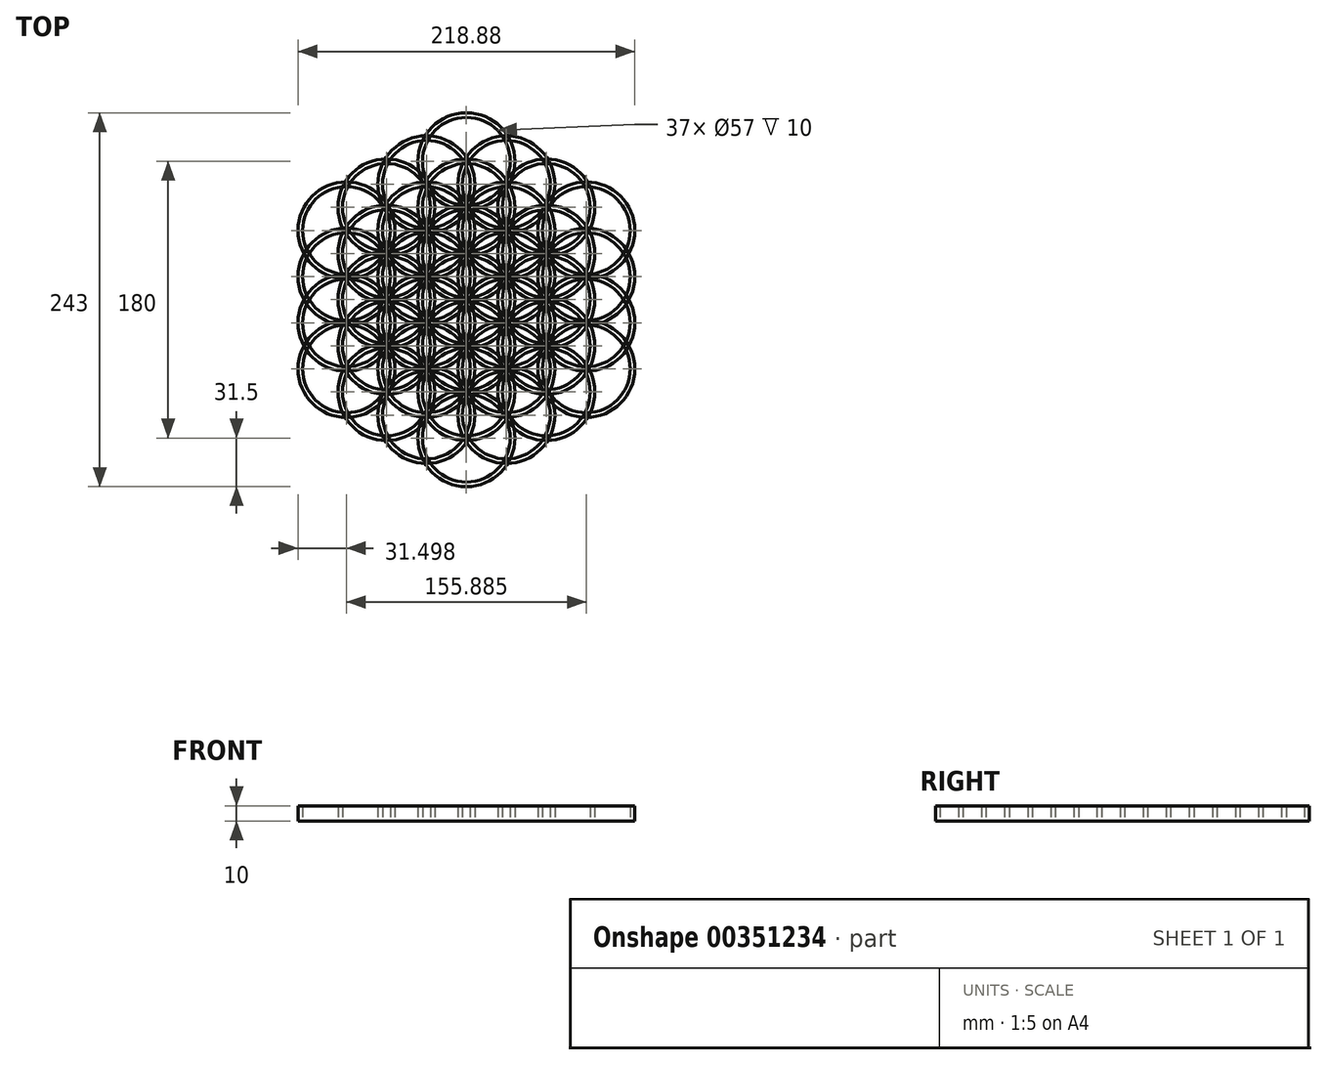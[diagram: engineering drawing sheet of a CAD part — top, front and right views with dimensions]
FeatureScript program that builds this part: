
annotation { "Feature Type Name" : "Feature", "Feature Type Description" : "" }
export const myFeature = defineFeature(function(context is Context, id is Id, definition is map)
    precondition{}
    {
        {
            var Q0;
            Q0=qCreatedBy(makeId("Right.planeOp"),FACE);
            var sketch = newSketch(context, id + "F0", { "sketchPlane" : qUnion([Q0])});
            skLineSegment(sketch, "E0", {"start": v(0, 0) * mm, "end": v(0, -9.37) * mm});
            skSolve(sketch);
        }
        {
            var Q0;
            Q0=qCreatedBy(makeId("Top.planeOp"),FACE);
            var sketch = newSketch(context, id + "F1", { "sketchPlane" : qUnion([Q0])});
            skCircle(sketch, "E1", {"center": v(0, 0) * mm, "radius": 30 * mm, "construction": true});
            skCircle(sketch, "E2.0", {"center": v(0, 0) * mm, "radius": 31.5 * mm});
            skCircle(sketch, "E3.0", {"center": v(0, 0) * mm, "radius": 28.5 * mm});
            skSolve(sketch);
        }
        {
            var Q0;
            Q0=makeQuery(id+"F1.imprint","IMPRINT",FACE,{"disambiguationData":[TD([[makeQuery(id+"F1.imprint","IMPRINT",EDGE,{"derivedFrom":sQuery(id+"F1.wireOp",EDGE,"E2.0")}),1.0]])]});
            extrude(context, id + "F2", {"entities" : qUnion([Q0]), "depth" : 10 * mm});
        }
        {
            var Q0;
            Q0=qCreatedBy(makeId("Top.planeOp"),FACE);
            var sketch = newSketch(context, id + "F3", { "sketchPlane" : qUnion([Q0])});
            skCircle(sketch, "E4", {"center": v(0, 30) * mm, "radius": 30 * mm, "construction": true});
            skCircle(sketch, "E5.0", {"center": v(0, 30) * mm, "radius": 31.5 * mm});
            skCircle(sketch, "E6.0", {"center": v(0, 30) * mm, "radius": 28.5 * mm});
            skCircle(sketch, "E7", {"center": v(0, 0) * mm, "radius": 30 * mm, "construction": true});
            skCircle(sketch, "E8.0", {"center": v(0, 0) * mm, "radius": 31.5 * mm, "construction": true});
            skCircle(sketch, "E9.0", {"center": v(0, 0) * mm, "radius": 28.5 * mm, "construction": true});
            skSolve(sketch);
        }
        {
            var Q0;
            Q0=qSketchRegion(id+"F3",true);
            extrude(context, id + "F4", {"entities" : qUnion([Q0]), "depth" : 10 * mm});
        }
        {
            var Q0;
            Q0=makeQuery(id+"F4.opExtrude","SWEPT_BODY",BODY,{"disambiguationData":[OSD([sQuery(id+"F3.wireOp",EDGE,"E5.0"),sQuery(id+"F3.wireOp",EDGE,"E6.0")])]});
            var Q1;
            Q1=sQuery(id+"F0.wireOp",EDGE,"E0");
            circularPattern(context, id + "F5", {"entities" : qUnion([Q0]), "axis" : qUnion([Q1]), "angle" : 360 * degree, "instanceCount" : 6, "equalSpace" : true});
        }
        {
            var Q0;
            Q0=qCreatedBy(makeId("Top.planeOp"),FACE);
            var sketch = newSketch(context, id + "F6", { "sketchPlane" : qUnion([Q0])});
            skCircle(sketch, "E10", {"center": v(0, 0) * mm, "radius": 30 * mm, "construction": true});
            skCircle(sketch, "E11.0", {"center": v(0, 0) * mm, "radius": 31.5 * mm, "construction": true});
            skCircle(sketch, "E12.0", {"center": v(0, 0) * mm, "radius": 28.5 * mm, "construction": true});
            skCircle(sketch, "E13", {"center": v(0, 30) * mm, "radius": 30 * mm, "construction": true});
            skCircle(sketch, "E14.0", {"center": v(0, 30) * mm, "radius": 31.5 * mm, "construction": true});
            skCircle(sketch, "E15.0", {"center": v(0, 30) * mm, "radius": 28.5 * mm, "construction": true});
            skCircle(sketch, "E16", {"center": v(-25.98, 15) * mm, "radius": 30 * mm, "construction": true});
            skCircle(sketch, "E17.0", {"center": v(-25.98, 15) * mm, "radius": 31.5 * mm, "construction": true});
            skCircle(sketch, "E18.0", {"center": v(-25.98, 15) * mm, "radius": 28.5 * mm, "construction": true});
            skCircle(sketch, "E19", {"center": v(-25.98, 45) * mm, "radius": 30 * mm, "construction": true});
            skCircle(sketch, "E20.0", {"center": v(-25.98, 45) * mm, "radius": 31.5 * mm});
            skCircle(sketch, "E21.0", {"center": v(-25.98, 45) * mm, "radius": 28.5 * mm});
            skSolve(sketch);
        }
        {
            var Q0;
            Q0=makeQuery(id+"F6.imprint","IMPRINT",FACE,{"disambiguationData":[TD([[makeQuery(id+"F6.imprint","IMPRINT",EDGE,{"derivedFrom":sQuery(id+"F6.wireOp",EDGE,"E20.0")}),1.0]])]});
            extrude(context, id + "F7", {"entities" : qUnion([Q0]), "depth" : 10 * mm});
        }
        {
            var Q0;
            Q0=makeQuery(id+"F7.opExtrude","SWEPT_BODY",BODY,{"disambiguationData":[OSD([sQuery(id+"F6.wireOp",EDGE,"E20.0"),sQuery(id+"F6.wireOp",EDGE,"E21.0")])]});
            var Q1;
            Q1=sQuery(id+"F0.wireOp",EDGE,"E0");
            circularPattern(context, id + "F8", {"entities" : qUnion([Q0]), "axis" : qUnion([Q1]), "angle" : 360 * degree, "instanceCount" : 6, "equalSpace" : true});
        }
        {
            var Q0;
            Q0=qCreatedBy(makeId("Top.planeOp"),FACE);
            var sketch = newSketch(context, id + "F9", { "sketchPlane" : qUnion([Q0])});
            skCircle(sketch, "E22", {"center": v(0, 0) * mm, "radius": 30 * mm, "construction": true});
            skCircle(sketch, "E23.0", {"center": v(0, 0) * mm, "radius": 31.5 * mm, "construction": true});
            skCircle(sketch, "E24.0", {"center": v(0, 0) * mm, "radius": 28.5 * mm, "construction": true});
            skCircle(sketch, "E25", {"center": v(0, 30) * mm, "radius": 30 * mm, "construction": true});
            skCircle(sketch, "E26.0", {"center": v(0, 30) * mm, "radius": 31.5 * mm, "construction": true});
            skCircle(sketch, "E27.0", {"center": v(0, 30) * mm, "radius": 28.5 * mm, "construction": true});
            skCircle(sketch, "E28", {"center": v(-25.98, 15) * mm, "radius": 30 * mm, "construction": true});
            skCircle(sketch, "E29.0", {"center": v(-25.98, 15) * mm, "radius": 31.5 * mm, "construction": true});
            skCircle(sketch, "E30.0", {"center": v(-25.98, 15) * mm, "radius": 28.5 * mm, "construction": true});
            skCircle(sketch, "E31", {"center": v(-25.98, 45) * mm, "radius": 30 * mm, "construction": true});
            skCircle(sketch, "E32.0", {"center": v(-25.98, 45) * mm, "radius": 31.5 * mm, "construction": true});
            skCircle(sketch, "E33.0", {"center": v(-25.98, 45) * mm, "radius": 28.5 * mm, "construction": true});
            skCircle(sketch, "E34", {"center": v(-80.96, 35.25) * mm, "radius": 20 * mm, "construction": true});
            skCircle(sketch, "E35.0", {"center": v(-80.96, 35.25) * mm, "radius": 21.5 * mm, "construction": true});
            skCircle(sketch, "E36.0", {"center": v(-80.96, 35.25) * mm, "radius": 18.5 * mm, "construction": true});
            skCircle(sketch, "E37", {"center": v(-51.96, 30) * mm, "radius": 30 * mm, "construction": true});
            skCircle(sketch, "E38.0", {"center": v(-51.96, 30) * mm, "radius": 31.5 * mm});
            skCircle(sketch, "E39.0", {"center": v(-51.96, 30) * mm, "radius": 28.5 * mm});
            skSolve(sketch);
        }
        {
            var Q0;
            Q0=makeQuery(id+"F9.imprint","IMPRINT",FACE,{"disambiguationData":[TD([[makeQuery(id+"F9.imprint","IMPRINT",EDGE,{"derivedFrom":sQuery(id+"F9.wireOp",EDGE,"E38.0")}),1.0]])]});
            extrude(context, id + "F10", {"entities" : qUnion([Q0]), "depth" : 10 * mm});
        }
        {
            var Q0;
            Q0=makeQuery(id+"F10.opExtrude","SWEPT_BODY",BODY,{"disambiguationData":[OSD([sQuery(id+"F9.wireOp",EDGE,"E38.0"),sQuery(id+"F9.wireOp",EDGE,"E39.0")])]});
            var Q1;
            Q1=sQuery(id+"F0.wireOp",EDGE,"E0");
            circularPattern(context, id + "F11", {"entities" : qUnion([Q0]), "axis" : qUnion([Q1]), "angle" : 360 * degree, "instanceCount" : 6, "equalSpace" : true});
        }
        {
            var Q0;
            Q0=qCreatedBy(makeId("Top.planeOp"),FACE);
            var sketch = newSketch(context, id + "F12", { "sketchPlane" : qUnion([Q0])});
            skCircle(sketch, "E40", {"center": v(0, 0) * mm, "radius": 30 * mm, "construction": true});
            skCircle(sketch, "E41.0", {"center": v(0, 0) * mm, "radius": 31.5 * mm, "construction": true});
            skCircle(sketch, "E42.0", {"center": v(0, 0) * mm, "radius": 28.5 * mm, "construction": true});
            skCircle(sketch, "E43", {"center": v(0, 30) * mm, "radius": 30 * mm, "construction": true});
            skCircle(sketch, "E44.0", {"center": v(0, 30) * mm, "radius": 31.5 * mm, "construction": true});
            skCircle(sketch, "E45.0", {"center": v(0, 30) * mm, "radius": 28.5 * mm, "construction": true});
            skCircle(sketch, "E46", {"center": v(-25.98, 15) * mm, "radius": 30 * mm, "construction": true});
            skCircle(sketch, "E47.0", {"center": v(-25.98, 15) * mm, "radius": 31.5 * mm, "construction": true});
            skCircle(sketch, "E48.0", {"center": v(-25.98, 15) * mm, "radius": 28.5 * mm, "construction": true});
            skCircle(sketch, "E49", {"center": v(-25.98, 45) * mm, "radius": 30 * mm, "construction": true});
            skCircle(sketch, "E50.0", {"center": v(-25.98, 45) * mm, "radius": 31.5 * mm, "construction": true});
            skCircle(sketch, "E51.0", {"center": v(-25.98, 45) * mm, "radius": 28.5 * mm, "construction": true});
            skCircle(sketch, "E52", {"center": v(-51.96, 60) * mm, "radius": 30 * mm, "construction": true});
            skCircle(sketch, "E53.0", {"center": v(-51.96, 60) * mm, "radius": 31.5 * mm});
            skCircle(sketch, "E54.0", {"center": v(-51.96, 60) * mm, "radius": 28.5 * mm});
            skCircle(sketch, "E55", {"center": v(-51.96, 30) * mm, "radius": 30 * mm, "construction": true});
            skCircle(sketch, "E56.0", {"center": v(-51.96, 30) * mm, "radius": 31.5 * mm, "construction": true});
            skCircle(sketch, "E57.0", {"center": v(-51.96, 30) * mm, "radius": 28.5 * mm, "construction": true});
            skSolve(sketch);
        }
        {
            var Q0;
            Q0=makeQuery(id+"F12.imprint","IMPRINT",FACE,{"disambiguationData":[TD([[makeQuery(id+"F12.imprint","IMPRINT",EDGE,{"derivedFrom":sQuery(id+"F12.wireOp",EDGE,"E53.0")}),1.0]])]});
            extrude(context, id + "F13", {"entities" : qUnion([Q0]), "depth" : 10 * mm});
        }
        {
            var Q0;
            Q0=makeQuery(id+"F13.opExtrude","SWEPT_BODY",BODY,{"disambiguationData":[OSD([sQuery(id+"F12.wireOp",EDGE,"E53.0"),sQuery(id+"F12.wireOp",EDGE,"E54.0")])]});
            var Q1;
            Q1=sQuery(id+"F0.wireOp",EDGE,"E0");
            circularPattern(context, id + "F14", {"entities" : qUnion([Q0]), "axis" : qUnion([Q1]), "angle" : 360 * degree, "instanceCount" : 6, "equalSpace" : true});
        }
        {
            var Q0;
            Q0=qCreatedBy(makeId("Top.planeOp"),FACE);
            var sketch = newSketch(context, id + "F15", { "sketchPlane" : qUnion([Q0])});
            skCircle(sketch, "E58", {"center": v(0, 0) * mm, "radius": 30 * mm, "construction": true});
            skCircle(sketch, "E59.0", {"center": v(0, 0) * mm, "radius": 31.5 * mm, "construction": true});
            skCircle(sketch, "E60.0", {"center": v(0, 0) * mm, "radius": 28.5 * mm, "construction": true});
            skCircle(sketch, "E61", {"center": v(0, 30) * mm, "radius": 30 * mm, "construction": true});
            skCircle(sketch, "E62.0", {"center": v(0, 30) * mm, "radius": 31.5 * mm, "construction": true});
            skCircle(sketch, "E63.0", {"center": v(0, 30) * mm, "radius": 28.5 * mm, "construction": true});
            skCircle(sketch, "E64", {"center": v(-25.98, 15) * mm, "radius": 30 * mm, "construction": true});
            skCircle(sketch, "E65.0", {"center": v(-25.98, 15) * mm, "radius": 31.5 * mm, "construction": true});
            skCircle(sketch, "E66.0", {"center": v(-25.98, 15) * mm, "radius": 28.5 * mm, "construction": true});
            skCircle(sketch, "E67", {"center": v(-25.98, 45) * mm, "radius": 30 * mm, "construction": true});
            skCircle(sketch, "E68.0", {"center": v(-25.98, 45) * mm, "radius": 31.5 * mm, "construction": true});
            skCircle(sketch, "E69.0", {"center": v(-25.98, 45) * mm, "radius": 28.5 * mm, "construction": true});
            skCircle(sketch, "E70", {"center": v(-51.96, 60) * mm, "radius": 30 * mm, "construction": true});
            skCircle(sketch, "E71.0", {"center": v(-51.96, 60) * mm, "radius": 31.5 * mm, "construction": true});
            skCircle(sketch, "E72.0", {"center": v(-51.96, 60) * mm, "radius": 28.5 * mm, "construction": true});
            skCircle(sketch, "E73", {"center": v(-51.96, 30) * mm, "radius": 30 * mm, "construction": true});
            skCircle(sketch, "E74.0", {"center": v(-51.96, 30) * mm, "radius": 31.5 * mm, "construction": true});
            skCircle(sketch, "E75.0", {"center": v(-51.96, 30) * mm, "radius": 28.5 * mm, "construction": true});
            skCircle(sketch, "E76", {"center": v(-25.98, 75) * mm, "radius": 30 * mm, "construction": true});
            skCircle(sketch, "E77.0", {"center": v(-25.98, 75) * mm, "radius": 31.5 * mm});
            skCircle(sketch, "E78.0", {"center": v(-25.98, 75) * mm, "radius": 28.5 * mm});
            skSolve(sketch);
        }
        {
            var Q0;
            Q0=makeQuery(id+"F15.imprint","IMPRINT",FACE,{"disambiguationData":[TD([[makeQuery(id+"F15.imprint","IMPRINT",EDGE,{"derivedFrom":sQuery(id+"F15.wireOp",EDGE,"E77.0")}),1.0]])]});
            extrude(context, id + "F16", {"entities" : qUnion([Q0]), "depth" : 10 * mm});
        }
        {
            var Q0;
            Q0=makeQuery(id+"F16.opExtrude","SWEPT_BODY",BODY,{"disambiguationData":[OSD([sQuery(id+"F15.wireOp",EDGE,"E77.0"),sQuery(id+"F15.wireOp",EDGE,"E78.0")])]});
            var Q1;
            Q1=sQuery(id+"F0.wireOp",EDGE,"E0");
            circularPattern(context, id + "F17", {"entities" : qUnion([Q0]), "axis" : qUnion([Q1]), "angle" : 360 * degree, "instanceCount" : 6, "equalSpace" : true});
        }
        {
            var Q0;
            Q0=qCreatedBy(makeId("Top.planeOp"),FACE);
            var sketch = newSketch(context, id + "F18", { "sketchPlane" : qUnion([Q0])});
            skCircle(sketch, "E79", {"center": v(0, 0) * mm, "radius": 30 * mm, "construction": true});
            skCircle(sketch, "E80.0", {"center": v(0, 0) * mm, "radius": 31.5 * mm, "construction": true});
            skCircle(sketch, "E81.0", {"center": v(0, 0) * mm, "radius": 28.5 * mm, "construction": true});
            skCircle(sketch, "E82", {"center": v(0, 30) * mm, "radius": 30 * mm, "construction": true});
            skCircle(sketch, "E83.0", {"center": v(0, 30) * mm, "radius": 31.5 * mm, "construction": true});
            skCircle(sketch, "E84.0", {"center": v(0, 30) * mm, "radius": 28.5 * mm, "construction": true});
            skCircle(sketch, "E85", {"center": v(-25.98, 15) * mm, "radius": 30 * mm, "construction": true});
            skCircle(sketch, "E86.0", {"center": v(-25.98, 15) * mm, "radius": 31.5 * mm, "construction": true});
            skCircle(sketch, "E87.0", {"center": v(-25.98, 15) * mm, "radius": 28.5 * mm, "construction": true});
            skCircle(sketch, "E88", {"center": v(-25.98, 45) * mm, "radius": 30 * mm, "construction": true});
            skCircle(sketch, "E89.0", {"center": v(-25.98, 45) * mm, "radius": 31.5 * mm, "construction": true});
            skCircle(sketch, "E90.0", {"center": v(-25.98, 45) * mm, "radius": 28.5 * mm, "construction": true});
            skCircle(sketch, "E91", {"center": v(-51.96, 60) * mm, "radius": 30 * mm, "construction": true});
            skCircle(sketch, "E92.0", {"center": v(-51.96, 60) * mm, "radius": 31.5 * mm, "construction": true});
            skCircle(sketch, "E93.0", {"center": v(-51.96, 60) * mm, "radius": 28.5 * mm, "construction": true});
            skCircle(sketch, "E94", {"center": v(-51.96, 30) * mm, "radius": 30 * mm, "construction": true});
            skCircle(sketch, "E95.0", {"center": v(-51.96, 30) * mm, "radius": 31.5 * mm, "construction": true});
            skCircle(sketch, "E96.0", {"center": v(-51.96, 30) * mm, "radius": 28.5 * mm, "construction": true});
            skCircle(sketch, "E97", {"center": v(-25.98, 75) * mm, "radius": 30 * mm, "construction": true});
            skCircle(sketch, "E98.0", {"center": v(-25.98, 75) * mm, "radius": 31.5 * mm, "construction": true});
            skCircle(sketch, "E99.0", {"center": v(-25.98, 75) * mm, "radius": 28.5 * mm, "construction": true});
            skCircle(sketch, "E100", {"center": v(0, 90) * mm, "radius": 30 * mm, "construction": true});
            skCircle(sketch, "E101.0", {"center": v(0, 90) * mm, "radius": 31.5 * mm});
            skCircle(sketch, "E102.0", {"center": v(0, 90) * mm, "radius": 28.5 * mm});
            skSolve(sketch);
        }
        {
            var Q0;
            Q0=makeQuery(id+"F18.imprint","IMPRINT",FACE,{"disambiguationData":[TD([[makeQuery(id+"F18.imprint","IMPRINT",EDGE,{"derivedFrom":sQuery(id+"F18.wireOp",EDGE,"E101.0")}),1.0]])]});
            extrude(context, id + "F19", {"entities" : qUnion([Q0]), "depth" : 10 * mm});
        }
        {
            var Q0;
            Q0=makeQuery(id+"F19.opExtrude","SWEPT_BODY",BODY,{"disambiguationData":[OSD([sQuery(id+"F18.wireOp",EDGE,"E101.0"),sQuery(id+"F18.wireOp",EDGE,"E102.0")])]});
            var Q1;
            Q1=sQuery(id+"F0.wireOp",EDGE,"E0");
            circularPattern(context, id + "F20", {"entities" : qUnion([Q0]), "axis" : qUnion([Q1]), "angle" : 360 * degree, "instanceCount" : 6, "equalSpace" : true});
        }
    });
